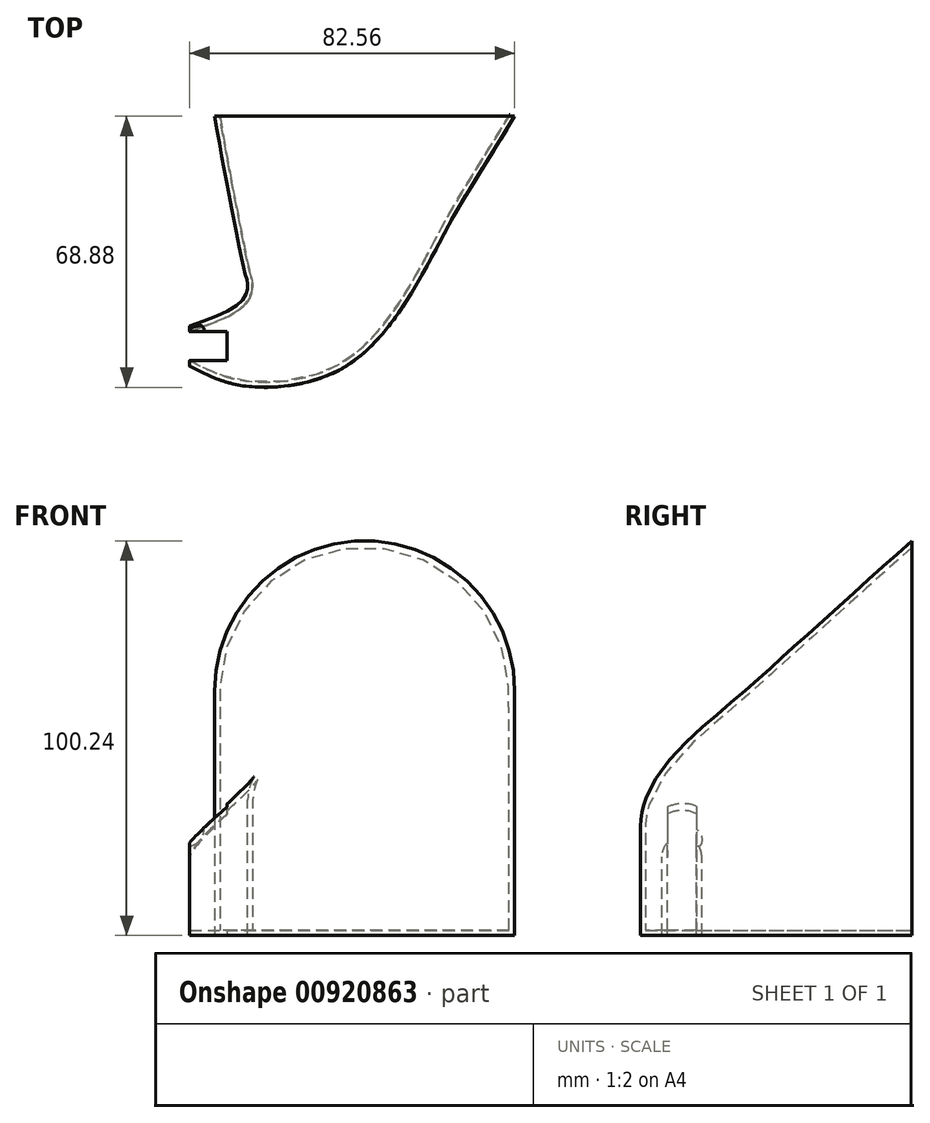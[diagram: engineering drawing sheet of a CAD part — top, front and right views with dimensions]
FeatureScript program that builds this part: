
annotation { "Feature Type Name" : "Feature", "Feature Type Description" : "" }
export const myFeature = defineFeature(function(context is Context, id is Id, definition is map)
    precondition{}
    {
        {
            var Q0;
            Q0=qCreatedBy(makeId("Top.planeOp"),FACE);
            var sketch = newSketch(context, id + "F0", { "sketchPlane" : qUnion([Q0])});
            skLineSegment(sketch, "E0", {"start": v(-82.55, 63.5) * mm, "end": v(-6.35, 63.5) * mm});
            skLineSegment(sketch, "E1", {"start": v(0, 0) * mm, "end": v(-19.05, 0) * mm});
            skFitSpline(sketch, "E2", {"points": [v(-19.05, 0) * mm, v(-37.46, 7.66) * mm, v(-49.92, 23.44) * mm, v(-67.16, 49.4) * mm, v(-82.55, 63.5) * mm], "startDerivative": vector(-86.21, 5.24) * mm, "endDerivative": vector(-66.51, 55.23) * mm});
            skFitSpline(sketch, "E3", {"points": [v(-6.35, 63.5) * mm, v(-19.69, 44.52) * mm, v(-21.66, 15.13) * mm, v(-10.55, 10.16) * mm], "startDerivative": vector(-42.8, -44.91) * mm, "endDerivative": vector(51.97, -8.72) * mm});
            skLineSegment(sketch, "E4", {"start": v(-10.55, 10.16) * mm, "end": v(0, 10.16) * mm});
            skLineSegment(sketch, "E5", {"start": v(0, 10.16) * mm, "end": v(0, 0) * mm});
            skSolve(sketch);
        }
        {
            var Q0;
            Q0=qCreatedBy(makeId("Right.planeOp"),FACE);
            var sketch = newSketch(context, id + "F1", { "sketchPlane" : qUnion([Q0])});
            skLineSegment(sketch, "E6.bottom", {"start": v(0, 0) * mm, "end": v(10.16, 0) * mm});
            skLineSegment(sketch, "E6.top", {"start": v(0, 19.95) * mm, "end": v(10.16, 19.95) * mm, "construction": true});
            skLineSegment(sketch, "E6.left", {"start": v(0, 0) * mm, "end": v(0, 19.95) * mm});
            skLineSegment(sketch, "E6.right", {"start": v(10.16, 0) * mm, "end": v(10.16, 19.95) * mm});
            skArc(sketch, "E7", {"start": v(10.16, 19.95) * mm, "mid": v(5.08, 25.03) * mm, "end": v(0, 19.95) * mm});
            skSolve(sketch);
        }
        {
            var Q0;
            Q0=sQuery(id+"F0.wireOp",VERTEX,"E0.start");
            var Q1;
            Q1=qCreatedBy(makeId("Front.planeOp"),FACE);
            cPlane(context, id + "F2", {"entities" : qUnion([Q0, Q1]), "cplaneType" : CPlaneType.PLANE_POINT, "offset" : 25.4 * mm, "width" : 152.4 * mm, "height" : 152.4 * mm});
        }
        {
            var Q0;
            Q0=qCreatedBy(id+"F2.planeOp",FACE);
            var sketch = newSketch(context, id + "F3", { "sketchPlane" : qUnion([Q0])});
            skLineSegment(sketch, "E8.bottom", {"start": v(-6.35, 0) * mm, "end": v(-82.55, 0) * mm});
            skLineSegment(sketch, "E8.top", {"start": v(-6.35, 62.14) * mm, "end": v(-82.55, 62.14) * mm, "construction": true});
            skLineSegment(sketch, "E8.left", {"start": v(-6.35, 0) * mm, "end": v(-6.35, 62.14) * mm});
            skLineSegment(sketch, "E8.right", {"start": v(-82.55, 0) * mm, "end": v(-82.55, 62.14) * mm});
            skArc(sketch, "E9", {"start": v(-6.35, 62.14) * mm, "mid": v(-44.45, 100.24) * mm, "end": v(-82.55, 62.14) * mm});
            skSolve(sketch);
        }
        {
            var Q0;
            Q0=qCreatedBy(makeId("Top.planeOp"),FACE);
            var sketch = newSketch(context, id + "F4", { "sketchPlane" : qUnion([Q0])});
            skLineSegment(sketch, "E10", {"start": v(-23.58, 0.68) * mm, "end": v(-18.27, 12.07) * mm, "construction": true});
            skLineSegment(sketch, "E11", {"start": v(-42.55, 12.73) * mm, "end": v(-23.53, 22.65) * mm, "construction": true});
            skLineSegment(sketch, "E12", {"start": v(-59.2, 38.43) * mm, "end": v(-20.12, 43.36) * mm, "construction": true});
            skLineSegment(sketch, "E13", {"start": v(-6.35, 63.5) * mm, "end": v(-82.55, 63.5) * mm});
            skLineSegment(sketch, "E14", {"start": v(0, 0) * mm, "end": v(0, 10.16) * mm, "construction": true});
            skFitSpline(sketch, "E15", {"points": [v(0, 5.08) * mm, v(-20.93, 6.38) * mm, v(-33.04, 17.69) * mm, v(-39.66, 40.9) * mm, v(-44.45, 63.5) * mm], "startDerivative": vector(-90.24, -5.22) * mm, "endDerivative": vector(-18.36, 84.36) * mm});
            skSolve(sketch);
        }
        {
            var Q0;
            Q0=sQuery(id+"F4.wireOp",EDGE,"E15");
            var Q1;
            Q1=makeQuery(id+"F1.imprint","IMPRINT",FACE,{"disambiguationData":[TD([[makeQuery(id+"F1.imprint","IMPRINT",EDGE,{"derivedFrom":sQuery(id+"F1.wireOp",EDGE,"E6.bottom")}),1.0]])]});
            var Q2;
            Q2=makeQuery(id+"F3.imprint","IMPRINT",FACE,{"disambiguationData":[TD([[makeQuery(id+"F3.imprint","IMPRINT",EDGE,{"derivedFrom":sQuery(id+"F3.wireOp",EDGE,"E8.bottom")}),-1.0]])]});
            loft(context, id + "F5", {"addSections" : true, "spine" : qUnion([Q0]), "sectionCount" : 5, "sheetProfilesArray" : [{ "sheetProfileEntities" : qUnion([Q1]) }, { "sheetProfileEntities" : qUnion([Q2]) }]});
        }
        {
            var Q0;
            Q0=makeQuery(id+"F5.opLoft","CAP_FACE",FACE,{"disambiguationData":[OSD([makeQuery(id+"F1.imprint","IMPRINT",FACE,{"disambiguationData":[TD([[makeQuery(id+"F1.imprint","IMPRINT",EDGE,{"derivedFrom":sQuery(id+"F1.wireOp",EDGE,"E6.bottom")}),1.0]])]})])],"isStart":true});
            var Q1;
            Q1=makeQuery(id+"F5.opLoft","CAP_FACE",FACE,{"disambiguationData":[OSD([makeQuery(id+"F3.imprint","IMPRINT",FACE,{"disambiguationData":[TD([[makeQuery(id+"F3.imprint","IMPRINT",EDGE,{"derivedFrom":sQuery(id+"F3.wireOp",EDGE,"E8.bottom")}),-1.0]])]})])],"isStart":true});
            shell(context, id + "F6", {"entities" : qUnion([Q0, Q1]), "thickness" : 1.27 * mm});
        }
        {
            var Q0;
            Q0=makeQuery(id+"F5.opLoft","SWEPT_FACE",FACE,{"disambiguationData":[OSD([sQuery(id+"F1.wireOp",EDGE,"E6.bottom"),sQuery(id+"F1.wireOp",EDGE,"E6.left"),sQuery(id+"F1.wireOp",EDGE,"E6.right"),sQuery(id+"F3.wireOp",EDGE,"E8.bottom"),sQuery(id+"F3.wireOp",EDGE,"E8.left"),sQuery(id+"F3.wireOp",EDGE,"E8.right")])]});
            var sketch = newSketch(context, id + "F7", { "sketchPlane" : qUnion([Q0])});
            skLineSegment(sketch, "E16.bottom", {"start": v(0, -1.45) * mm, "end": v(-9.52, -1.45) * mm});
            skLineSegment(sketch, "E16.top", {"start": v(0, -8.81) * mm, "end": v(-9.52, -8.81) * mm});
            skLineSegment(sketch, "E16.left", {"start": v(0, -1.45) * mm, "end": v(0, -8.81) * mm});
            skLineSegment(sketch, "E16.right", {"start": v(-9.53, -1.45) * mm, "end": v(-9.52, -8.81) * mm});
            skSolve(sketch);
        }
        {
            var Q0;
            Q0=qSketchRegion(id+"F7",true);
            extrude(context, id + "F8", {"entities" : qUnion([Q0]), "operationType" : NewBodyOperationType.REMOVE, "oppositeDirection" : true, "depth" : 50.8 * mm, "offsetDistance" : 25.4 * mm});
        }
        {
            var Q0;
            Q0=makeQuery(id+"F5.opLoft","SWEPT_BODY",BODY,{"disambiguationData":[OSD([makeQuery(id+"F1.imprint","IMPRINT",FACE,{"disambiguationData":[TD([[makeQuery(id+"F1.imprint","IMPRINT",EDGE,{"derivedFrom":sQuery(id+"F1.wireOp",EDGE,"E6.bottom")}),1.0]])]}),makeQuery(id+"F3.imprint","IMPRINT",FACE,{"disambiguationData":[TD([[makeQuery(id+"F3.imprint","IMPRINT",EDGE,{"derivedFrom":sQuery(id+"F3.wireOp",EDGE,"E8.bottom")}),-1.0]])]})])]});
            var Q1;
            Q1=qCreatedBy(makeId("Right.planeOp"),FACE);
            mirror(context, id + "F9", {"operationType" : NewBodyOperationType.ADD, "entities" : qUnion([Q0]), "mirrorPlane" : qUnion([Q1])});
        }
        {
            var Q0;
            Q0=qCreatedBy(makeId("Top.planeOp"),FACE);
            var sketch = newSketch(context, id + "F10", { "sketchPlane" : qUnion([Q0])});
            skLineSegment(sketch, "E17.bottom", {"start": v(0, 73.68) * mm, "end": v(-94.65, 73.68) * mm});
            skLineSegment(sketch, "E17.top", {"start": v(0, -29.62) * mm, "end": v(-94.65, -29.62) * mm});
            skLineSegment(sketch, "E17.left", {"start": v(0, 73.68) * mm, "end": v(0, -29.62) * mm});
            skLineSegment(sketch, "E17.right", {"start": v(-94.65, 73.68) * mm, "end": v(-94.65, -29.62) * mm});
            skSolve(sketch);
        }
        {
            var Q0;
            Q0=makeQuery(id+"F10.imprint","IMPRINT",FACE,{"disambiguationData":[TD([[makeQuery(id+"F10.imprint","IMPRINT",EDGE,{"derivedFrom":sQuery(id+"F10.wireOp",EDGE,"E17.bottom")}),1.0]])]});
            extrude(context, id + "F11", {"entities" : qUnion([Q0]), "operationType" : NewBodyOperationType.REMOVE, "endBound" : BoundingType.THROUGH_ALL, "depth" : 25.4 * mm, "offsetDistance" : 25.4 * mm});
        }
        {
            var Q0;
            {var subQ0=sQuery(id+"F3.wireOp",EDGE,"E9");var subQ1=sQuery(id+"F3.wireOp",EDGE,"E8.right");var subQ2=sQuery(id+"F3.wireOp",EDGE,"E8.bottom");var subQ3=sQuery(id+"F1.wireOp",EDGE,"E7");var subQ4=sQuery(id+"F1.wireOp",EDGE,"E6.left");var subQ5=sQuery(id+"F1.wireOp",EDGE,"E6.bottom");var subQ6=makeQuery(id+"F8.boolean.opBoolean","COPY",FACE,{"disambiguationData":[TD([makeQuery(id+"F5.opLoft","SWEPT_FACE",FACE,{"disambiguationData":[OSD([subQ5,subQ4,subQ3,subQ2,subQ1,subQ0])]})])],"derivedFrom":makeQuery(id+"F8.opExtrude","SWEPT_FACE",FACE,{"disambiguationData":[OSD([sQuery(id+"F7.wireOp",EDGE,"E16.bottom")])]})});Q0=makeQuery(id+"F9.boolean.opBoolean","MERGE",FACE,{"derivedFrom":[subQ6,makeQuery(id+"F9.opPattern","COPY",FACE,{"derivedFrom":subQ6,"instanceName":"1"})]});}
            var sketch = newSketch(context, id + "F12", { "sketchPlane" : qUnion([Q0])});
            skCircle(sketch, "E18", {"center": v(0.94, 27.13) * mm, "radius": 4.6 * mm});
            skSolve(sketch);
        }
        {
            var Q0;
            Q0 = qSketchRegion(id + "F12", true);
            extrude(context, id + "F13", {"entities" : qUnion([Q0]), "operationType" : NewBodyOperationType.REMOVE, "depth" : 25.4 * mm, "offsetDistance" : 25.4 * mm});
        }
    });
